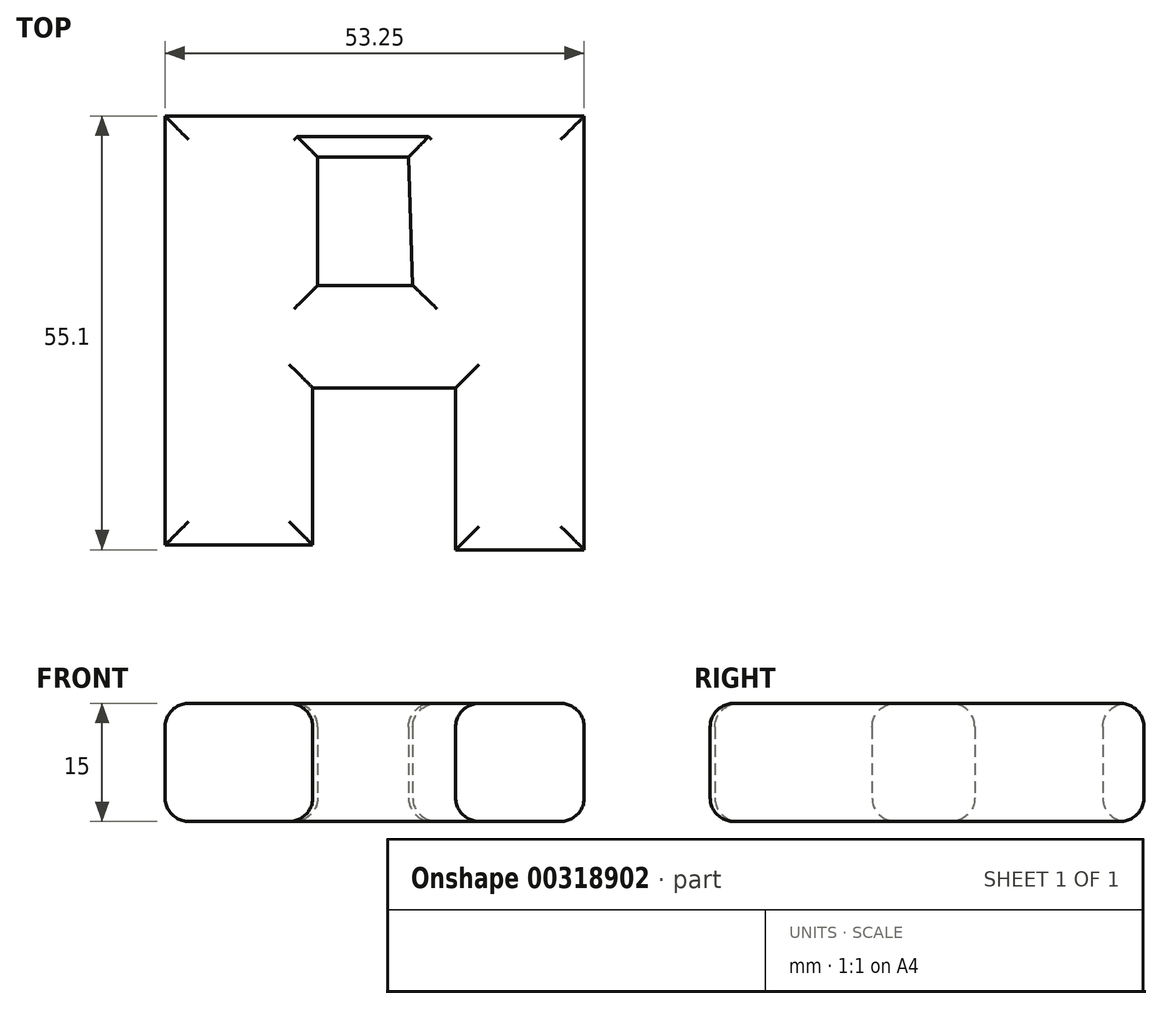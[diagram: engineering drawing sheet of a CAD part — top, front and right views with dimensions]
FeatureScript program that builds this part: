
annotation { "Feature Type Name" : "Feature", "Feature Type Description" : "" }
export const myFeature = defineFeature(function(context is Context, id is Id, definition is map)
    precondition{}
    {
        {
            var Q0;
            Q0=qCreatedBy(makeId("Top.planeOp"),FACE);
            var sketch = newSketch(context, id + "F0", { "sketchPlane" : qUnion([Q0])});
            skLineSegment(sketch, "E0", {"start": v(0, 0) * mm, "end": v(-28.8, 0) * mm});
            skLineSegment(sketch, "E1", {"start": v(-28.8, 0) * mm, "end": v(-28.8, -54.5) * mm});
            skLineSegment(sketch, "E2", {"start": v(-28.8, -54.5) * mm, "end": v(-10.05, -54.5) * mm});
            skLineSegment(sketch, "E3", {"start": v(-10.05, -54.5) * mm, "end": v(-10.05, -34.53) * mm});
            skLineSegment(sketch, "E4", {"start": v(-10.05, -34.53) * mm, "end": v(8.1, -34.53) * mm});
            skLineSegment(sketch, "E5", {"start": v(8.1, -34.53) * mm, "end": v(8.1, -55.1) * mm});
            skLineSegment(sketch, "E6", {"start": v(8.1, -55.1) * mm, "end": v(24.44, -55.1) * mm});
            skLineSegment(sketch, "E7", {"start": v(24.44, -55.1) * mm, "end": v(24.44, 0) * mm});
            skLineSegment(sketch, "E8", {"start": v(24.44, 0) * mm, "end": v(-25.78, 0) * mm});
            skLineSegment(sketch, "E9", {"start": v(-25.78, 0) * mm, "end": v(-28.8, 0) * mm});
            skLineSegment(sketch, "E10", {"start": v(2.13, -5.22) * mm, "end": v(-9.42, -5.22) * mm});
            skLineSegment(sketch, "E11", {"start": v(-9.42, -5.22) * mm, "end": v(-9.42, -21.5) * mm});
            skLineSegment(sketch, "E12", {"start": v(-9.42, -21.5) * mm, "end": v(2.66, -21.5) * mm});
            skLineSegment(sketch, "E13", {"start": v(2.66, -21.5) * mm, "end": v(2.13, -5.22) * mm});
            skSolve(sketch);
        }
        {
            var Q0;
            Q0=makeQuery(id+"F0.imprint","IMPRINT",FACE,{"disambiguationData":[TD([[makeQuery(id+"F0.imprint","IMPRINT",EDGE,{"derivedFrom":sQuery(id+"F0.wireOp",EDGE,"E1")}),1.0]])]});
            extrude(context, id + "F1", {"entities" : qUnion([Q0]), "depth" : 15 * mm});
        }
        {
            var Q0;
            Q0=makeQuery(id+"F1.opExtrude","CAP_FACE",FACE,{"disambiguationData":[OSD([sQuery(id+"F0.wireOp",EDGE,"E1"),sQuery(id+"F0.wireOp",EDGE,"E2"),sQuery(id+"F0.wireOp",EDGE,"E3"),sQuery(id+"F0.wireOp",EDGE,"E4"),sQuery(id+"F0.wireOp",EDGE,"E5"),sQuery(id+"F0.wireOp",EDGE,"E6"),sQuery(id+"F0.wireOp",EDGE,"E7"),sQuery(id+"F0.wireOp",EDGE,"E8"),sQuery(id+"F0.wireOp",EDGE,"E9"),sQuery(id+"F0.wireOp",EDGE,"E11"),sQuery(id+"F0.wireOp",EDGE,"E12"),sQuery(id+"F0.wireOp",EDGE,"E13"),sQuery(id+"F0.wireOp",EDGE,"E10")])],"isStart":false});
            var Q1;
            Q1=makeQuery(id+"F1.opExtrude","CAP_FACE",FACE,{"disambiguationData":[OSD([sQuery(id+"F0.wireOp",EDGE,"E1"),sQuery(id+"F0.wireOp",EDGE,"E2"),sQuery(id+"F0.wireOp",EDGE,"E3"),sQuery(id+"F0.wireOp",EDGE,"E4"),sQuery(id+"F0.wireOp",EDGE,"E5"),sQuery(id+"F0.wireOp",EDGE,"E6"),sQuery(id+"F0.wireOp",EDGE,"E7"),sQuery(id+"F0.wireOp",EDGE,"E8"),sQuery(id+"F0.wireOp",EDGE,"E9"),sQuery(id+"F0.wireOp",EDGE,"E11"),sQuery(id+"F0.wireOp",EDGE,"E12"),sQuery(id+"F0.wireOp",EDGE,"E13"),sQuery(id+"F0.wireOp",EDGE,"E10")])],"isStart":true});
            fillet(context, id + "F2", {"entities" : qUnion([Q0, Q1]), "radius" : 3 * mm, "tangentPropagation" : true, "allowEdgeOverflow" : false});
        }
    });
